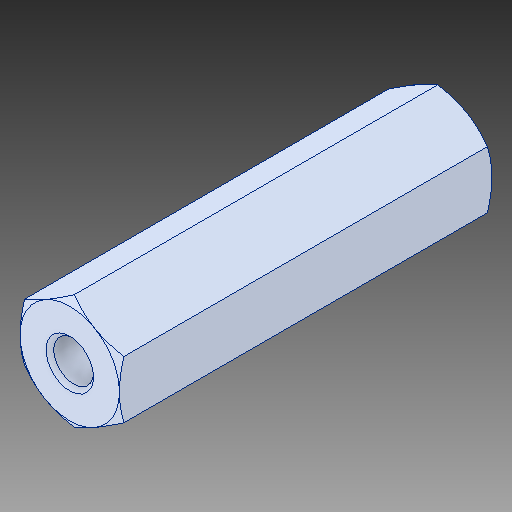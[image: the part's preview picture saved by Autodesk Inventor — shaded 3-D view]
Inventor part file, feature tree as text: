
AUTODESK INVENTOR PART (.ipt)
format: ipt  version: 2017 (Build 210142000, 142)  size: 123,904 bytes
history: native  units: in
note: dims shown in document units (in); Inventor stores cm internally (conversion verified against a paired STEP export)
features: chamfer x1
ambient origin geometry x8: Origin, YZ Plane, XZ Plane, XY Plane, X Axis, Y Axis, Z Axis, Center Point
bodies: Solid1 (feature_tree)
feature tree (1):
  chamfer  "Chamfer1"  [1 undecoded]
note: 1 required parameter value undecoded (feature->parameter linkage not recoverable at this tier; creation-order binding heuristic only, values carry confidence <= 0.55)
